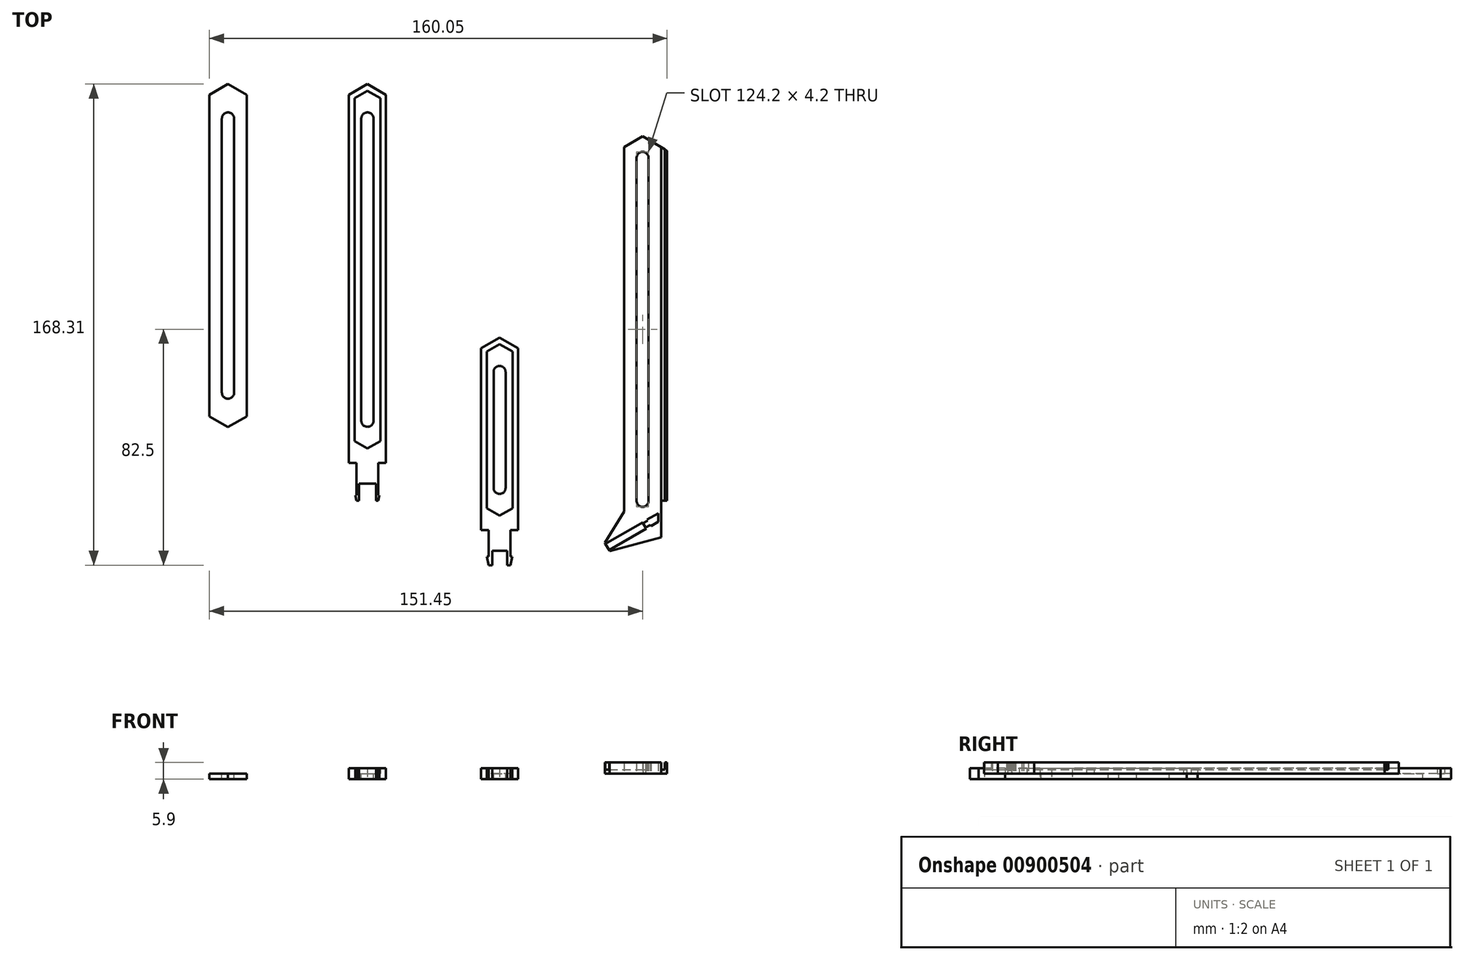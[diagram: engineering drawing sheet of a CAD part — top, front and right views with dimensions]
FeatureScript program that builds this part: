
annotation { "Feature Type Name" : "Feature", "Feature Type Description" : "" }
export const myFeature = defineFeature(function(context is Context, id is Id, definition is map)
    precondition{}
    {
        {
            var Q0;
            Q0=qCreatedBy(makeId("Top.planeOp"),FACE);
            var sketch = newSketch(context, id + "F0", { "sketchPlane" : qUnion([Q0])});
            skLineSegment(sketch, "E0", {"start": v(0, 0) * mm, "end": v(0.8, 0) * mm});
            skLineSegment(sketch, "E1", {"start": v(7.6, 2) * mm, "end": v(7.6, 13.3) * mm});
            skLineSegment(sketch, "E2", {"start": v(0, 13.3) * mm, "end": v(0, 2) * mm});
            skLineSegment(sketch, "E3", {"start": v(0, 2) * mm, "end": v(7.6, 2) * mm, "construction": true});
            skLineSegment(sketch, "E4", {"start": v(7.6, 13.3) * mm, "end": v(0, 13.3) * mm, "construction": true});
            skLineSegment(sketch, "E5", {"start": v(3.8, 120) * mm, "end": v(3.8, 13.3) * mm, "construction": true});
            skLineSegment(sketch, "E6", {"start": v(0, 13.3) * mm, "end": v(7.6, 13.3) * mm});
            skLineSegment(sketch, "E7", {"start": v(7.6, 2) * mm, "end": v(8, 2) * mm});
            skLineSegment(sketch, "E8", {"start": v(8, 2) * mm, "end": v(7.6, 0) * mm});
            skLineSegment(sketch, "E9", {"start": v(6.8, 0) * mm, "end": v(6.8, 6) * mm});
            skLineSegment(sketch, "E10", {"start": v(6.8, 6) * mm, "end": v(3.8, 6) * mm});
            skLineSegment(sketch, "E11.MirrorCS", {"start": v(0.8, 6) * mm, "end": v(3.8, 6) * mm});
            skLineSegment(sketch, "E12.MirrorCS", {"start": v(0.8, 0) * mm, "end": v(0.8, 6) * mm});
            skLineSegment(sketch, "E13.MirrorCS", {"start": v(7.6, 0) * mm, "end": v(6.8, 0) * mm});
            skLineSegment(sketch, "E14.MirrorCS", {"start": v(-0.4, 2) * mm, "end": v(0, 0) * mm});
            skLineSegment(sketch, "E15.MirrorCS", {"start": v(0, 2) * mm, "end": v(-0.4, 2) * mm});
            skLineSegment(sketch, "E16.trimOffspring", {"start": v(0.8, 0) * mm, "end": v(0, 0) * mm});
            skLineSegment(sketch, "E17.trimOffspring", {"start": v(6.8, 0) * mm, "end": v(7.6, 0) * mm});
            skCircle(sketch, "E18.cCircle", {"center": v(3.8, 23.5) * mm, "radius": 4.5 * mm, "construction": true});
            skLineSegment(sketch, "E18.0", {"start": v(8.3, 26.1) * mm, "end": v(8.3, 20.9) * mm});
            skLineSegment(sketch, "E18.1", {"start": v(8.3, 20.9) * mm, "end": v(3.8, 18.3) * mm});
            skLineSegment(sketch, "E18.2", {"start": v(3.8, 18.3) * mm, "end": v(-0.7, 20.9) * mm});
            skLineSegment(sketch, "E18.3", {"start": v(-0.7, 20.9) * mm, "end": v(-0.7, 46.1) * mm});
            skLineSegment(sketch, "E18.5", {"start": v(3.8, 28.7) * mm, "end": v(3.8, 28.7) * mm});
            skPoint(sketch, "E18.0.midPoint", {"position": v(8.3, 23.5) * mm});
            skCircle(sketch, "E19.cCircle", {"center": v(3.8, 138.3) * mm, "radius": 4.5 * mm, "construction": true});
            skLineSegment(sketch, "E19.0", {"start": v(8.3, 140.9) * mm, "end": v(8.3, 135.7) * mm});
            skLineSegment(sketch, "E19.3", {"start": v(-0.7, 135.7) * mm, "end": v(-0.7, 140.9) * mm});
            skLineSegment(sketch, "E19.4", {"start": v(-0.7, 140.9) * mm, "end": v(3.8, 143.5) * mm});
            skLineSegment(sketch, "E19.5", {"start": v(3.8, 143.5) * mm, "end": v(8.3, 140.9) * mm});
            skPoint(sketch, "E19.0.midPoint", {"position": v(8.3, 138.3) * mm});
            skLineSegment(sketch, "E20", {"start": v(8.3, 26.1) * mm, "end": v(8.3, 135.7) * mm});
            skLineSegment(sketch, "E21", {"start": v(-0.7, 46.1) * mm, "end": v(-0.7, 135.7) * mm});
            skLineSegment(sketch, "E22.0", {"start": v(10.3, 46.1) * mm, "end": v(10.3, 13.3) * mm});
            skLineSegment(sketch, "E22.1", {"start": v(10.3, 46.1) * mm, "end": v(10.3, 135.7) * mm});
            skLineSegment(sketch, "E22.2", {"start": v(10.3, 142.05) * mm, "end": v(10.3, 135.7) * mm});
            skLineSegment(sketch, "E22.3", {"start": v(3.8, 145.8) * mm, "end": v(10.3, 142.05) * mm});
            skLineSegment(sketch, "E22.4", {"start": v(-2.7, 13.3) * mm, "end": v(-2.7, 26.1) * mm});
            skLineSegment(sketch, "E22.5", {"start": v(-2.7, 26.1) * mm, "end": v(-2.7, 135.7) * mm});
            skLineSegment(sketch, "E22.6", {"start": v(-2.7, 135.7) * mm, "end": v(-2.7, 142.05) * mm});
            skLineSegment(sketch, "E22.7", {"start": v(-2.7, 142.05) * mm, "end": v(3.8, 145.8) * mm});
            skLineSegment(sketch, "E23", {"start": v(0, 13.3) * mm, "end": v(-2.7, 13.3) * mm});
            skLineSegment(sketch, "E24", {"start": v(7.6, 13.3) * mm, "end": v(10.3, 13.3) * mm});
            skArc(sketch, "E25", {"start": v(1.65, 28.05) * mm, "mid": v(3.8, 25.9) * mm, "end": v(5.95, 28.05) * mm});
            skArc(sketch, "E26", {"start": v(5.95, 133.75) * mm, "mid": v(3.8, 135.9) * mm, "end": v(1.65, 133.75) * mm});
            skLineSegment(sketch, "E27", {"start": v(1.65, 28.05) * mm, "end": v(1.65, 133.75) * mm});
            skLineSegment(sketch, "E28.MirrorCS", {"start": v(5.95, 28.05) * mm, "end": v(5.95, 133.75) * mm});
            skLineSegment(sketch, "E29", {"start": v(-2.7, 17.3) * mm, "end": v(10.3, 17.3) * mm});
            skLineSegment(sketch, "E30", {"start": v(-17.65, 151.2) * mm, "end": v(-17.65, -8.95) * mm, "construction": true});
            skLineSegment(sketch, "E31", {"start": v(-11.5, 85.8) * mm, "end": v(-75.72, 85.8) * mm, "construction": true});
            skCircle(sketch, "E32.cCircle", {"center": v(-44.95, 138.3) * mm, "radius": 4.5 * mm, "construction": true});
            skLineSegment(sketch, "E32.0", {"start": v(-40.45, 140.9) * mm, "end": v(-40.45, 135.7) * mm});
            skLineSegment(sketch, "E32.3", {"start": v(-49.45, 135.7) * mm, "end": v(-49.45, 140.9) * mm});
            skLineSegment(sketch, "E32.4", {"start": v(-49.45, 140.9) * mm, "end": v(-44.95, 143.5) * mm});
            skLineSegment(sketch, "E32.5", {"start": v(-44.95, 143.5) * mm, "end": v(-40.45, 140.9) * mm});
            skPoint(sketch, "E32.0.midPoint", {"position": v(-40.45, 138.3) * mm});
            skLineSegment(sketch, "E33", {"start": v(-40.45, 85.8) * mm, "end": v(-40.45, 135.7) * mm});
            skLineSegment(sketch, "E34", {"start": v(-49.45, 85.8) * mm, "end": v(-49.45, 135.7) * mm});
            skLineSegment(sketch, "E35.1", {"start": v(-38.45, 85.8) * mm, "end": v(-38.45, 135.7) * mm});
            skLineSegment(sketch, "E35.2", {"start": v(-38.45, 142.05) * mm, "end": v(-38.45, 135.7) * mm});
            skLineSegment(sketch, "E35.3", {"start": v(-44.95, 145.8) * mm, "end": v(-38.45, 142.05) * mm});
            skLineSegment(sketch, "E35.5", {"start": v(-51.45, 85.8) * mm, "end": v(-51.45, 135.7) * mm});
            skLineSegment(sketch, "E35.6", {"start": v(-51.45, 135.7) * mm, "end": v(-51.45, 142.05) * mm});
            skLineSegment(sketch, "E35.7", {"start": v(-51.45, 142.05) * mm, "end": v(-44.95, 145.8) * mm});
            skArc(sketch, "E36", {"start": v(-42.8, 133.75) * mm, "mid": v(-44.95, 135.9) * mm, "end": v(-47.1, 133.75) * mm});
            skLineSegment(sketch, "E37", {"start": v(-47.1, 85.8) * mm, "end": v(-47.1, 133.75) * mm});
            skLineSegment(sketch, "E38.MirrorCS", {"start": v(-42.8, 85.8) * mm, "end": v(-42.8, 133.75) * mm});
            skLineSegment(sketch, "E39.MirrorCS", {"start": v(-44.95, 28.11) * mm, "end": v(-40.45, 30.71) * mm});
            skLineSegment(sketch, "E40.MirrorCS", {"start": v(-40.45, 30.71) * mm, "end": v(-40.45, 35.9) * mm});
            skLineSegment(sketch, "E41.MirrorCS", {"start": v(-49.45, 30.71) * mm, "end": v(-44.95, 28.11) * mm});
            skLineSegment(sketch, "E42.MirrorCS", {"start": v(-49.45, 35.9) * mm, "end": v(-49.45, 30.71) * mm});
            skArc(sketch, "E43.MirrorCS", {"start": v(-42.8, 37.86) * mm, "mid": v(-44.95, 35.71) * mm, "end": v(-47.1, 37.86) * mm});
            skLineSegment(sketch, "E44.MirrorCS", {"start": v(-49.45, 85.8) * mm, "end": v(-49.45, 35.9) * mm});
            skLineSegment(sketch, "E45.MirrorCS", {"start": v(-51.45, 29.56) * mm, "end": v(-44.95, 25.8) * mm});
            skCircle(sketch, "E46.MirrorC", {"center": v(-44.95, 33.31) * mm, "radius": 4.5 * mm, "construction": true});
            skLineSegment(sketch, "E47.MirrorCS", {"start": v(-44.95, 25.8) * mm, "end": v(-38.45, 29.56) * mm});
            skLineSegment(sketch, "E48.MirrorCS", {"start": v(-42.8, 85.8) * mm, "end": v(-42.8, 37.86) * mm});
            skPoint(sketch, "E49.MirrorP", {"position": v(-40.45, 33.31) * mm});
            skLineSegment(sketch, "E50.MirrorCS", {"start": v(-40.45, 85.8) * mm, "end": v(-40.45, 35.9) * mm});
            skLineSegment(sketch, "E51.MirrorCS", {"start": v(-38.45, 29.56) * mm, "end": v(-38.45, 35.9) * mm});
            skLineSegment(sketch, "E52.MirrorCS", {"start": v(-38.45, 85.8) * mm, "end": v(-38.45, 35.9) * mm});
            skLineSegment(sketch, "E53.MirrorCS", {"start": v(-51.45, 35.9) * mm, "end": v(-51.45, 29.56) * mm});
            skLineSegment(sketch, "E54.MirrorCS", {"start": v(-47.1, 85.8) * mm, "end": v(-47.1, 37.86) * mm});
            skLineSegment(sketch, "E55.MirrorCS", {"start": v(-51.45, 85.8) * mm, "end": v(-51.45, 35.9) * mm});
            skCircle(sketch, "E56.cCircle", {"center": v(50, 0) * mm, "radius": 4.5 * mm, "construction": true});
            skLineSegment(sketch, "E56.0", {"start": v(45.5, -2.6) * mm, "end": v(45.5, 2.6) * mm});
            skLineSegment(sketch, "E56.3", {"start": v(54.5, 2.6) * mm, "end": v(54.5, -2.6) * mm});
            skLineSegment(sketch, "E56.4", {"start": v(54.5, -2.6) * mm, "end": v(50, -5.2) * mm});
            skLineSegment(sketch, "E56.5", {"start": v(50, -5.2) * mm, "end": v(45.5, -2.6) * mm});
            skPoint(sketch, "E56.0.midPoint", {"position": v(45.5, 0) * mm});
            skLineSegment(sketch, "E57", {"start": v(0, 0) * mm, "end": v(50, 0) * mm, "construction": true});
            skLineSegment(sketch, "E58", {"start": v(50, -22.27) * mm, "end": v(50, 200.86) * mm, "construction": true});
            skArc(sketch, "E59", {"start": v(47.9, 4.5) * mm, "mid": v(50, 2.4) * mm, "end": v(52.1, 4.5) * mm});
            skLineSegment(sketch, "E60", {"start": v(45.5, 2.6) * mm, "end": v(45.5, 24.8) * mm});
            skLineSegment(sketch, "E61", {"start": v(47.9, 4.5) * mm, "end": v(47.9, 24.8) * mm});
            skLineSegment(sketch, "E62", {"start": v(43.5, -10.2) * mm, "end": v(43.5, 24.8) * mm});
            skLineSegment(sketch, "E63", {"start": v(46.2, -10.2) * mm, "end": v(43.5, -10.2) * mm});
            skLineSegment(sketch, "E64", {"start": v(35.44, 24.8) * mm, "end": v(70.44, 24.8) * mm, "construction": true});
            skLineSegment(sketch, "E65.MirrorCS", {"start": v(52.1, 4.5) * mm, "end": v(52.1, 24.8) * mm});
            skLineSegment(sketch, "E66.MirrorCS", {"start": v(54.5, 2.6) * mm, "end": v(54.5, 24.8) * mm});
            skLineSegment(sketch, "E67.MirrorCS", {"start": v(56.5, -10.2) * mm, "end": v(56.5, 24.8) * mm});
            skLineSegment(sketch, "E68.MirrorCS", {"start": v(50, -10.2) * mm, "end": v(56.5, -10.2) * mm});
            skLineSegment(sketch, "E69.MirrorCS", {"start": v(43.5, 53.36) * mm, "end": v(43.5, 24.8) * mm});
            skLineSegment(sketch, "E70.MirrorCS", {"start": v(47.9, 45.1) * mm, "end": v(47.9, 24.8) * mm});
            skLineSegment(sketch, "E71.MirrorCS", {"start": v(45.5, 52.2) * mm, "end": v(45.5, 47) * mm});
            skLineSegment(sketch, "E72.MirrorCS", {"start": v(54.5, 52.2) * mm, "end": v(50, 54.8) * mm});
            skLineSegment(sketch, "E73.MirrorCS", {"start": v(56.5, 53.36) * mm, "end": v(56.5, 24.8) * mm});
            skLineSegment(sketch, "E74.MirrorCS", {"start": v(54.5, 47) * mm, "end": v(54.5, 24.8) * mm});
            skLineSegment(sketch, "E75.MirrorCS", {"start": v(52.1, 45.1) * mm, "end": v(52.1, 24.8) * mm});
            skPoint(sketch, "E76.MirrorP", {"position": v(45.5, 49.6) * mm});
            skCircle(sketch, "E77.MirrorC", {"center": v(50, 49.6) * mm, "radius": 4.5 * mm, "construction": true});
            skArc(sketch, "E78.MirrorC", {"start": v(47.9, 45.1) * mm, "mid": v(50, 47.2) * mm, "end": v(52.1, 45.1) * mm});
            skLineSegment(sketch, "E79.MirrorCS", {"start": v(45.5, 47) * mm, "end": v(45.5, 24.8) * mm});
            skLineSegment(sketch, "E80.MirrorCS", {"start": v(54.5, 47) * mm, "end": v(54.5, 52.2) * mm});
            skLineSegment(sketch, "E81.MirrorCS", {"start": v(50, 54.8) * mm, "end": v(45.5, 52.2) * mm});
            skLineSegment(sketch, "E82.MirrorCS", {"start": v(53.8, -10.2) * mm, "end": v(55.7, -10.2) * mm});
            skPoint(sketch, "E83.endSnap0", {"position": v(50, 89.3) * mm});
            skLineSegment(sketch, "E84.0", {"start": v(50, 57.11) * mm, "end": v(43.5, 53.36) * mm});
            skLineSegment(sketch, "E84.1", {"start": v(56.5, 53.36) * mm, "end": v(50, 57.11) * mm});
            skLineSegment(sketch, "E85", {"start": v(47.4, -10.2) * mm, "end": v(46.2, -10.2) * mm});
            skLineSegment(sketch, "E86", {"start": v(46.2, -10.2) * mm, "end": v(46.2, -19.5) * mm});
            skLineSegment(sketch, "E87", {"start": v(46.2, -19.5) * mm, "end": v(45.6, -19.5) * mm});
            skLineSegment(sketch, "E88", {"start": v(45.6, -19.5) * mm, "end": v(46.2, -22.5) * mm});
            skLineSegment(sketch, "E89", {"start": v(46.2, -22.5) * mm, "end": v(47.4, -22.5) * mm});
            skLineSegment(sketch, "E90", {"start": v(47.4, -22.5) * mm, "end": v(47.4, -17.5) * mm});
            skLineSegment(sketch, "E91.MirrorCS", {"start": v(53.8, -19.5) * mm, "end": v(54.4, -19.5) * mm});
            skLineSegment(sketch, "E92.MirrorCS", {"start": v(52.6, -10.2) * mm, "end": v(53.8, -10.2) * mm});
            skLineSegment(sketch, "E93.MirrorCS", {"start": v(54.4, -19.5) * mm, "end": v(53.8, -22.5) * mm});
            skLineSegment(sketch, "E94.MirrorCS", {"start": v(52.6, -10.2) * mm, "end": v(56.5, -10.2) * mm});
            skLineSegment(sketch, "E95.MirrorCS", {"start": v(52.6, -22.5) * mm, "end": v(52.6, -17.5) * mm});
            skLineSegment(sketch, "E96.MirrorCS", {"start": v(53.8, -22.5) * mm, "end": v(52.6, -22.5) * mm});
            skLineSegment(sketch, "E97.MirrorCS", {"start": v(53.8, -10.2) * mm, "end": v(53.8, -19.5) * mm});
            skLineSegment(sketch, "E98", {"start": v(47.4, -17.5) * mm, "end": v(52.6, -17.5) * mm});
            skPoint(sketch, "E99.orphan", {"position": v(50, -10.2) * mm});
            skLineSegment(sketch, "E100", {"start": v(50, 0) * mm, "end": v(100, 0) * mm, "construction": true});
            skPoint(sketch, "E100.endSnap0", {"position": v(54.5, 0) * mm});
            skLineSegment(sketch, "E101", {"start": v(100, -26.78) * mm, "end": v(100, 196.36) * mm, "construction": true});
            skArc(sketch, "E102", {"start": v(97.9, 0) * mm, "mid": v(100, -2.1) * mm, "end": v(102.1, 0) * mm});
            skLineSegment(sketch, "E103", {"start": v(97.9, 0) * mm, "end": v(97.9, 60) * mm});
            skLineSegment(sketch, "E104.MirrorCS", {"start": v(102.1, 0) * mm, "end": v(102.1, 60) * mm});
            skLineSegment(sketch, "E105", {"start": v(86.72, 60) * mm, "end": v(127.33, 60) * mm, "construction": true});
            skLineSegment(sketch, "E106.MirrorCS", {"start": v(102.1, 120) * mm, "end": v(102.1, 60) * mm});
            skLineSegment(sketch, "E107.MirrorCS", {"start": v(97.9, 120) * mm, "end": v(97.9, 60) * mm});
            skArc(sketch, "E108.MirrorC", {"start": v(97.9, 120) * mm, "mid": v(100, 122.1) * mm, "end": v(102.1, 120) * mm});
            skCircle(sketch, "E109.cCircle", {"center": v(100, 0) * mm, "radius": 6.5 * mm, "construction": true});
            skLineSegment(sketch, "E109.0", {"start": v(93.5, -3.75) * mm, "end": v(93.5, 3.75) * mm});
            skLineSegment(sketch, "E109.3", {"start": v(106.5, 3.75) * mm, "end": v(106.5, -4.21) * mm});
            skLineSegment(sketch, "E109.5", {"start": v(100, -7.5) * mm, "end": v(93.5, -3.75) * mm});
            skPoint(sketch, "E109.0.midPoint", {"position": v(93.5, 0) * mm});
            skLineSegment(sketch, "E110", {"start": v(106.5, 3.75) * mm, "end": v(106.5, 60) * mm});
            skLineSegment(sketch, "E111", {"start": v(93.5, 3.75) * mm, "end": v(93.5, 60) * mm});
            skLineSegment(sketch, "E112.MirrorCS", {"start": v(93.5, 116.25) * mm, "end": v(93.5, 60) * mm});
            skLineSegment(sketch, "E113.MirrorCS", {"start": v(106.5, 116.25) * mm, "end": v(106.5, 60) * mm});
            skLineSegment(sketch, "E114.MirrorCS", {"start": v(106.5, 116.25) * mm, "end": v(106.5, 123.75) * mm});
            skLineSegment(sketch, "E115.MirrorCS", {"start": v(106.5, 123.75) * mm, "end": v(100, 127.5) * mm});
            skLineSegment(sketch, "E116.MirrorCS", {"start": v(100, 127.5) * mm, "end": v(93.5, 123.75) * mm});
            skLineSegment(sketch, "E117.MirrorCS", {"start": v(93.5, 123.75) * mm, "end": v(93.5, 116.25) * mm});
            skLineSegment(sketch, "E118", {"start": v(87, -15) * mm, "end": v(86.8, -14.66) * mm});
            skLineSegment(sketch, "E119", {"start": v(86.8, -14.66) * mm, "end": v(93.5, -3.75) * mm});
            skLineSegment(sketch, "E120", {"start": v(87, -15) * mm, "end": v(88.3, -17.26) * mm});
            skLineSegment(sketch, "E121", {"start": v(88.3, -17.26) * mm, "end": v(101.3, -9.76) * mm});
            skLineSegment(sketch, "E122", {"start": v(106.5, -6.75) * mm, "end": v(106.5, -6.2) * mm});
            skLineSegment(sketch, "E123", {"start": v(106.5, -6.75) * mm, "end": v(106.5, -12.75) * mm});
            skLineSegment(sketch, "E124", {"start": v(106.5, -12.75) * mm, "end": v(88.5, -17.6) * mm});
            skLineSegment(sketch, "E125", {"start": v(88.5, -17.6) * mm, "end": v(88.3, -17.26) * mm});
            skLineSegment(sketch, "E126", {"start": v(100, -7.5) * mm, "end": v(101.3, -9.76) * mm});
            skLineSegment(sketch, "E127", {"start": v(100.2, -7.85) * mm, "end": v(101.8, -6.93) * mm});
            skLineSegment(sketch, "E128", {"start": v(102.66, -8.42) * mm, "end": v(101.06, -9.35) * mm});
            skPoint(sketch, "E129.orphan", {"position": v(106.5, -3.75) * mm});
            skLineSegment(sketch, "E130", {"start": v(106.5, -6.2) * mm, "end": v(106.5, -4.21) * mm});
            skLineSegment(sketch, "E131", {"start": v(87, -15) * mm, "end": v(100, -7.5) * mm});
            skLineSegment(sketch, "E132.0", {"start": v(105.5, -6.78) * mm, "end": v(105.5, -4.8) * mm});
            skLineSegment(sketch, "E133", {"start": v(106.5, 0) * mm, "end": v(108.6, 0) * mm});
            skLineSegment(sketch, "E134", {"start": v(108.6, 0) * mm, "end": v(108.6, 122.54) * mm});
            skLineSegment(sketch, "E135", {"start": v(108.6, 122.54) * mm, "end": v(106.5, 123.75) * mm});
            skLineSegment(sketch, "E136", {"start": v(107.8, 0) * mm, "end": v(107.8, 123) * mm});
            skLineSegment(sketch, "E137", {"start": v(101.6, -6.58) * mm, "end": v(105.5, -4.33) * mm});
            skLineSegment(sketch, "E138", {"start": v(105.5, -4.33) * mm, "end": v(105.5, -4.8) * mm});
            skLineSegment(sketch, "E139", {"start": v(102.9, -8.83) * mm, "end": v(105.5, -7.33) * mm});
            skLineSegment(sketch, "E140", {"start": v(105.5, -7.33) * mm, "end": v(105.5, -6.78) * mm});
            skLineSegment(sketch, "E141", {"start": v(102.66, -8.42) * mm, "end": v(102.9, -8.83) * mm});
            skLineSegment(sketch, "E142", {"start": v(101.8, -6.93) * mm, "end": v(101.6, -6.58) * mm});
            skSolve(sketch);
        }
        {
            var Q0;
            Q0=makeQuery(id+"F0.imprint","IMPRINT",FACE,{"disambiguationData":[TD([[makeQuery(id+"F0.imprint","IMPRINT",EDGE,{"derivedFrom":sQuery(id+"F0.wireOp",EDGE,"E0")}),1.0]])]});
            var Q1;
            Q1=makeQuery(id+"F0.imprint","IMPRINT",FACE,{"disambiguationData":[TD([[makeQuery(id+"F0.imprint","IMPRINT",EDGE,{"derivedFrom":sQuery(id+"F0.wireOp",EDGE,"1mUVOgRn-jnxG-UW5b-DkVR-PXYvtb08xrXX")}),1.0]])]});
            var Q2;
            {var subQ1=sQuery(id+"F0.wireOp",EDGE,"E6");Q2=makeQuery(id+"F0.imprint","IMPRINT",FACE,{"disambiguationData":[TD([[makeQuery(id+"F0.imprint","IMPRINT",EDGE,{"derivedFrom":subQ1}),-1.0]])]});}
            var Q3;
            Q3=makeQuery(id+"F0.imprint","IMPRINT",FACE,{"disambiguationData":[TD([[makeQuery(id+"F0.imprint","IMPRINT",EDGE,{"derivedFrom":sQuery(id+"F0.wireOp",EDGE,"E6")}),1.0]])]});
            var Q4;
            Q4=makeQuery(id+"F0.imprint","IMPRINT",FACE,{"disambiguationData":[TD([[makeQuery(id+"F0.imprint","IMPRINT",EDGE,{"derivedFrom":sQuery(id+"F0.wireOp",EDGE,"E18.0")}),1.0]])]});
            var Q5;
            Q5=makeQuery(id+"F0.imprint","IMPRINT",FACE,{"disambiguationData":[TD([[makeQuery(id+"F0.imprint","IMPRINT",EDGE,{"derivedFrom":sQuery(id+"F0.wireOp",EDGE,"E56.0")}),1.0]])]});
            extrude(context, id + "F1", {"entities" : qUnion([Q0, Q1, Q2, Q3, Q4, Q5]), "endBound" : BoundingType.SYMMETRIC, "depth" : 3.8 * mm, "offsetDistance" : 25 * mm});
        }
        {
            var Q0;
            Q0=makeQuery(id+"F0.imprint","IMPRINT",FACE,{"disambiguationData":[TD([[makeQuery(id+"F0.imprint","IMPRINT",EDGE,{"derivedFrom":sQuery(id+"F0.wireOp",EDGE,"E18.0")}),-1.0]])]});
            var Q1;
            Q1=makeQuery(id+"F0.imprint","IMPRINT",FACE,{"disambiguationData":[TD([[makeQuery(id+"F0.imprint","IMPRINT",EDGE,{"derivedFrom":sQuery(id+"F0.wireOp",EDGE,"E32.0")}),-1.0]])]});
            var Q2;
            Q2=makeQuery(id+"F0.imprint","IMPRINT",FACE,{"disambiguationData":[TD([[makeQuery(id+"F0.imprint","IMPRINT",EDGE,{"derivedFrom":sQuery(id+"F0.wireOp",EDGE,"E32.0")}),1.0]])]});
            var Q3;
            Q3=makeQuery(id+"F0.imprint","IMPRINT",FACE,{"disambiguationData":[TD([[makeQuery(id+"F0.imprint","IMPRINT",EDGE,{"derivedFrom":sQuery(id+"F0.wireOp",EDGE,"E56.0")}),-1.0]])]});
            extrude(context, id + "F2", {"entities" : qUnion([Q0, Q1, Q2, Q3]), "operationType" : NewBodyOperationType.ADD, "oppositeDirection" : true, "depth" : 1.9 * mm, "offsetDistance" : 25 * mm});
        }
        {
            var Q0;
            Q0=makeQuery(id+"F0.imprint","IMPRINT",FACE,{"disambiguationData":[TD([[makeQuery(id+"F0.imprint","IMPRINT",EDGE,{"derivedFrom":sQuery(id+"F0.wireOp",EDGE,"E102")}),-1.0]])]});
            var Q1;
            Q1=makeQuery(id+"F0.imprint","IMPRINT",FACE,{"disambiguationData":[TD([[makeQuery(id+"F0.imprint","IMPRINT",EDGE,{"derivedFrom":sQuery(id+"F0.wireOp",EDGE,"E109.5")}),1.0]])]});
            var Q2;
            {var subQ0=sQuery(id+"F0.wireOp",EDGE,"E123");Q2=makeQuery(id+"F0.imprint","IMPRINT",FACE,{"disambiguationData":[TD([[makeQuery(id+"F0.imprint","IMPRINT",EDGE,{"derivedFrom":subQ0}),-1.0]])]});}
            var Q3;
            {var subQ0=sQuery(id+"F0.wireOp",EDGE,"E134");Q3=makeQuery(id+"F0.imprint","IMPRINT",FACE,{"disambiguationData":[TD([[makeQuery(id+"F0.imprint","IMPRINT",EDGE,{"derivedFrom":subQ0}),1.0]])]});}
            extrude(context, id + "F3", {"entities" : qUnion([Q0, Q1, Q2, Q3]), "depth" : 4 * mm, "offsetDistance" : 25 * mm});
        }
        {
            var Q0;
            {var subQ1=sQuery(id+"F0.wireOp",EDGE,"E110");Q0=makeQuery(id+"F0.imprint","IMPRINT",FACE,{"disambiguationData":[TD([[makeQuery(id+"F0.imprint","IMPRINT",EDGE,{"derivedFrom":subQ1}),-1.0]])]});}
            var Q1;
            Q1=makeQuery(id+"F0.imprint","IMPRINT",FACE,{"disambiguationData":[TD([[makeQuery(id+"F0.imprint","IMPRINT",EDGE,{"derivedFrom":sQuery(id+"F0.wireOp",EDGE,"E120")}),1.0]])]});
            extrude(context, id + "F4", {"entities" : qUnion([Q0, Q1]), "operationType" : NewBodyOperationType.ADD, "depth" : 1.5 * mm, "offsetDistance" : 25 * mm});
        }
    });
